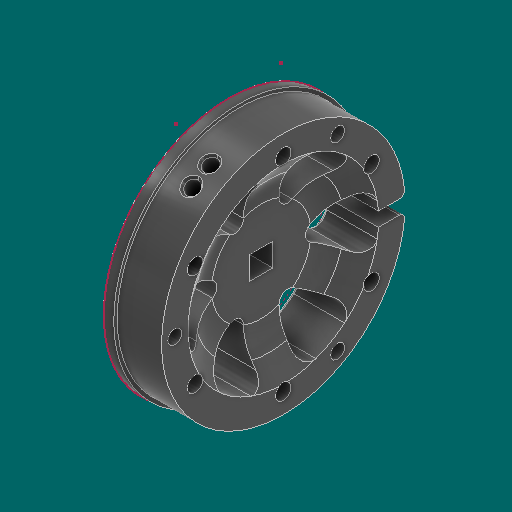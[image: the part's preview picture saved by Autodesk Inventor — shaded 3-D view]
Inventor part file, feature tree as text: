
AUTODESK INVENTOR PART (.ipt)
format: ipt  version: 2023.1 (Build 271208000, 208)  size: 549,376 bytes
history: native  units: in
note: dims shown in document units (in); Inventor stores cm internally (conversion verified against a paired STEP export)
features: sketch x5, other x3
ambient origin geometry x8: Origin, YZ Plane, XZ Plane, XY Plane, X Axis, Y Axis, Z Axis, Center Point
bodies: Solid1 (feature_tree)
feature tree (8):
  other  "WheelHalf.ipt"
  other  "Solid1::WheelHalf.ipt"
  other  "TaggingFeature1"
  sketch  "Sketch1"  dims[d0=0.3937in]
  sketch  "Sketch2"
  sketch  "Sketch3"
  sketch  "Sketch4"
  sketch  "Sketch5"
